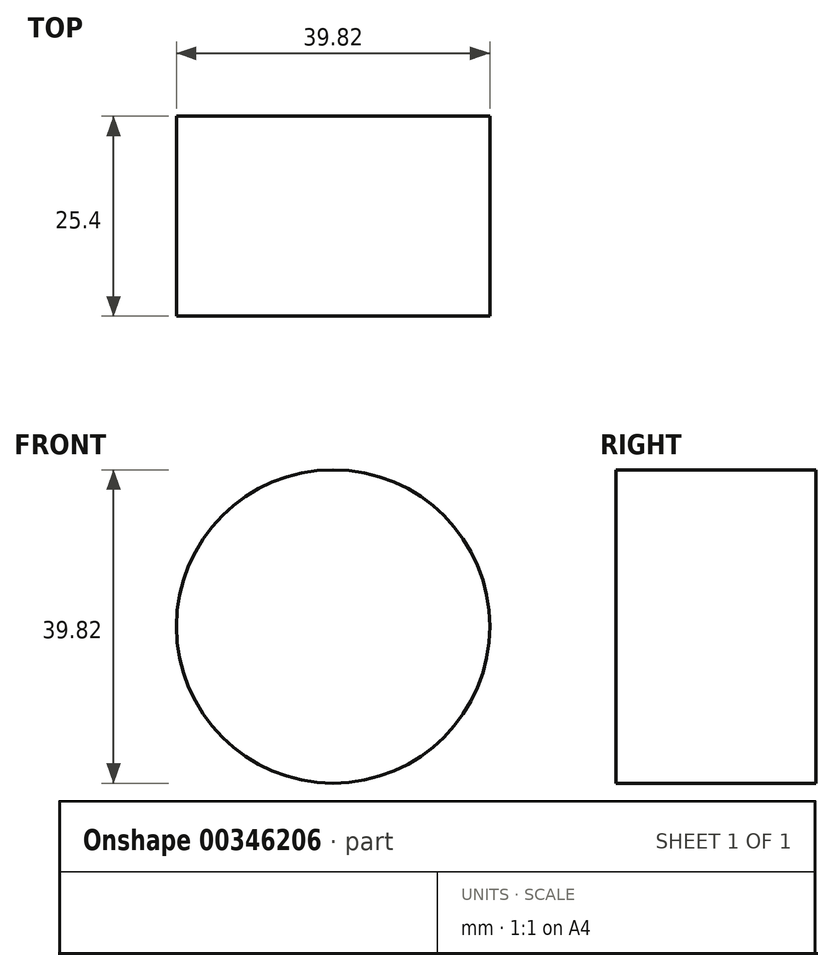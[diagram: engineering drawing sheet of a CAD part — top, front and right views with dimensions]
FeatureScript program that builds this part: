
annotation { "Feature Type Name" : "Feature", "Feature Type Description" : "" }
export const myFeature = defineFeature(function(context is Context, id is Id, definition is map)
    precondition{}
    {
        {
            var Q0;
            Q0=qCreatedBy(makeId("Front.planeOp"),FACE);
            var sketch = newSketch(context, id + "F0", { "sketchPlane" : qUnion([Q0])});
            skCircle(sketch, "E0", {"center": v(0, 0) * mm, "radius": 19.9 * mm});
            skSolve(sketch);
        }
        {
            var Q0;
            Q0 = qSketchRegion(id + "F0", true);
            extrude(context, id + "F1", {"entities" : qUnion([Q0]), "depth" : 25.4 * mm});
        }
    });
